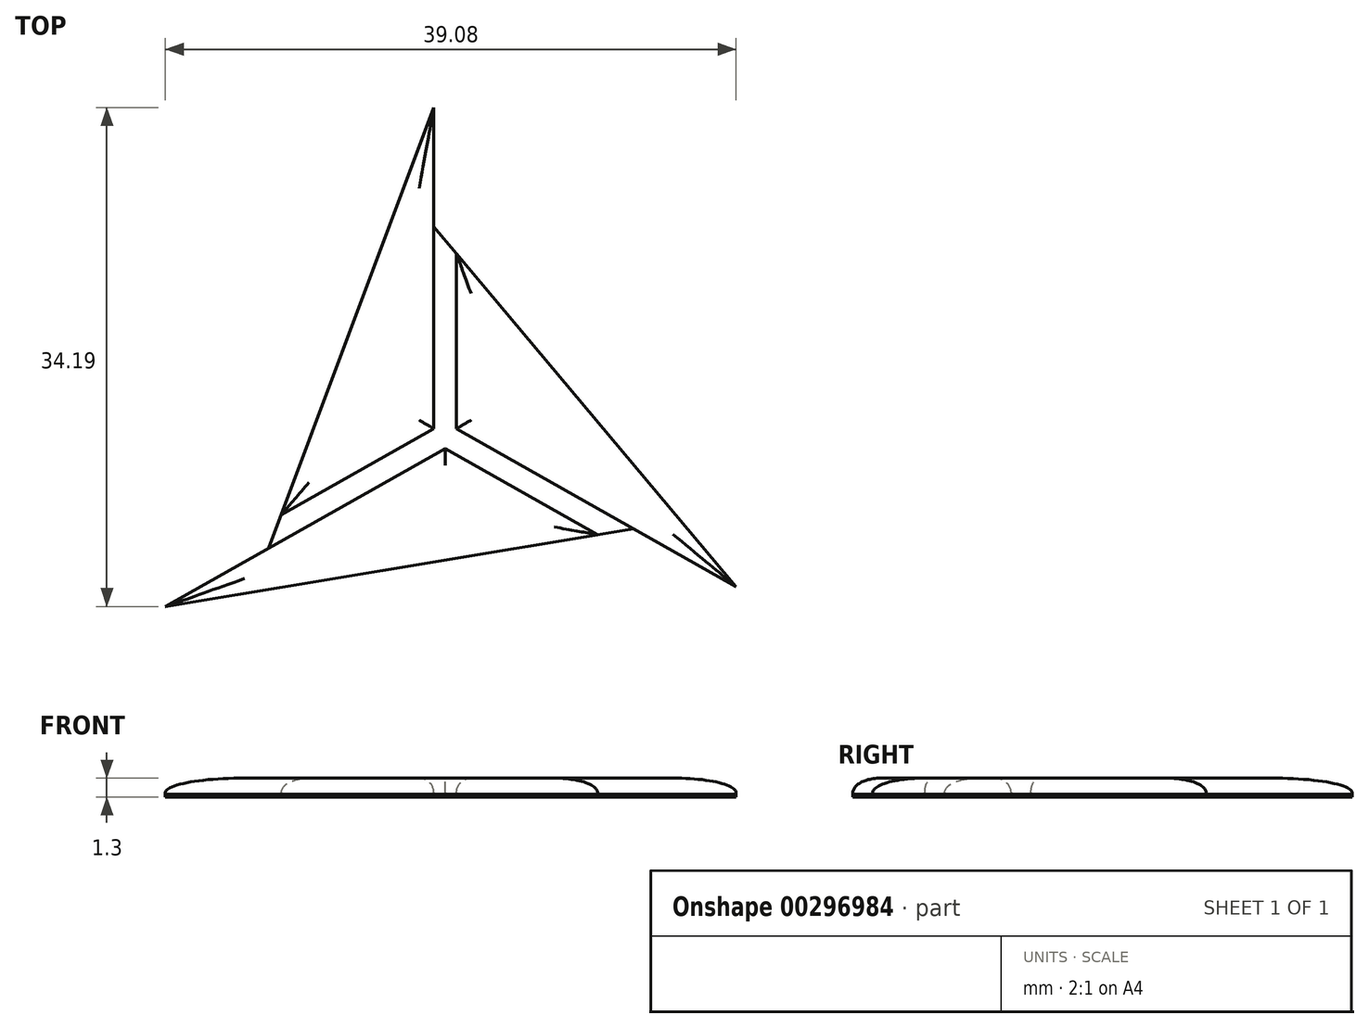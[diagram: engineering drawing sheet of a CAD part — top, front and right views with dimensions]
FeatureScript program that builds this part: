
annotation { "Feature Type Name" : "Feature", "Feature Type Description" : "" }
export const myFeature = defineFeature(function(context is Context, id is Id, definition is map)
    precondition{}
    {
        {
            var Q0;
            Q0=qCreatedBy(makeId("Top.planeOp"),FACE);
            var sketch = newSketch(context, id + "F0", { "sketchPlane" : qUnion([Q0])});
            skLineSegment(sketch, "E0", {"start": v(-11.18, -5.37) * mm, "end": v(-0.74, 22.54) * mm});
            skLineSegment(sketch, "E1", {"start": v(-0.74, 22.54) * mm, "end": v(-0.74, 0.54) * mm});
            skLineSegment(sketch, "E2", {"start": v(-0.74, 0.54) * mm, "end": v(-11.18, -5.37) * mm});
            skLineSegment(sketch, "E3", {"start": v(0.81, 12.54) * mm, "end": v(19.96, -10.3) * mm});
            skLineSegment(sketch, "E4", {"start": v(19.96, -10.3) * mm, "end": v(0.81, 0.54) * mm});
            skLineSegment(sketch, "E5", {"start": v(0.81, 0.54) * mm, "end": v(0.81, 12.54) * mm});
            skLineSegment(sketch, "E6", {"start": v(10.47, -6.72) * mm, "end": v(-19.12, -11.65) * mm});
            skLineSegment(sketch, "E7", {"start": v(-19.12, -11.65) * mm, "end": v(0.03, -0.82) * mm});
            skLineSegment(sketch, "E8", {"start": v(0.03, -0.82) * mm, "end": v(10.47, -6.72) * mm});
            skSolve(sketch);
        }
        {
            var Q0;
            Q0 = qSketchRegion(id + "F0", true);
            extrude(context, id + "F1", {"entities" : qUnion([Q0]), "depth" : 1.3 * mm, "offsetDistance" : 25 * mm});
        }
        {
            var Q0;
            Q0=makeQuery(id+"F1.opExtrude","CAP_FACE",FACE,{"disambiguationData":[OSD([sQuery(id+"F0.wireOp",EDGE,"E0"),sQuery(id+"F0.wireOp",EDGE,"E1"),sQuery(id+"F0.wireOp",EDGE,"E2")])],"isStart":false});
            var Q1;
            Q1=makeQuery(id+"F1.opExtrude","CAP_FACE",FACE,{"disambiguationData":[OSD([sQuery(id+"F0.wireOp",EDGE,"E3"),sQuery(id+"F0.wireOp",EDGE,"E4"),sQuery(id+"F0.wireOp",EDGE,"E5")])],"isStart":false});
            var Q2;
            Q2=makeQuery(id+"F1.opExtrude","CAP_FACE",FACE,{"disambiguationData":[OSD([sQuery(id+"F0.wireOp",EDGE,"E6"),sQuery(id+"F0.wireOp",EDGE,"E7"),sQuery(id+"F0.wireOp",EDGE,"E8")])],"isStart":false});
            fillet(context, id + "F2", {"entities" : qUnion([Q0, Q1, Q2]), "radius" : 1 * mm, "tangentPropagation" : true, "allowEdgeOverflow" : false});
        }
        {
            var Q0;
            Q0=makeQuery(id+"F1.opExtrude","CAP_FACE",FACE,{"disambiguationData":[OSD([sQuery(id+"F0.wireOp",EDGE,"E3"),sQuery(id+"F0.wireOp",EDGE,"E4"),sQuery(id+"F0.wireOp",EDGE,"E5")])],"isStart":true});
            var sketch = newSketch(context, id + "F3", { "sketchPlane" : qUnion([Q0])});
            skLineSegment(sketch, "E9", {"start": v(19.96, 10.3) * mm, "end": v(-0.74, -14.4) * mm});
            skLineSegment(sketch, "E10", {"start": v(-0.74, -14.4) * mm, "end": v(-0.74, -22.54) * mm});
            skLineSegment(sketch, "E11", {"start": v(-0.74, -22.54) * mm, "end": v(-12.04, 7.65) * mm});
            skLineSegment(sketch, "E12", {"start": v(-12.04, 7.65) * mm, "end": v(-19.12, 11.65) * mm});
            skLineSegment(sketch, "E13", {"start": v(-19.12, 11.65) * mm, "end": v(12.93, 6.31) * mm});
            skLineSegment(sketch, "E14", {"start": v(12.93, 6.31) * mm, "end": v(19.96, 10.3) * mm});
            skSolve(sketch);
        }
        {
            var Q0;
            Q0 = qSketchRegion(id + "F3", true);
            extrude(context, id + "F4", {"entities" : qUnion([Q0]), "oppositeDirection" : true, "depth" : 0.2 * mm, "offsetDistance" : 25 * mm});
        }
    });
